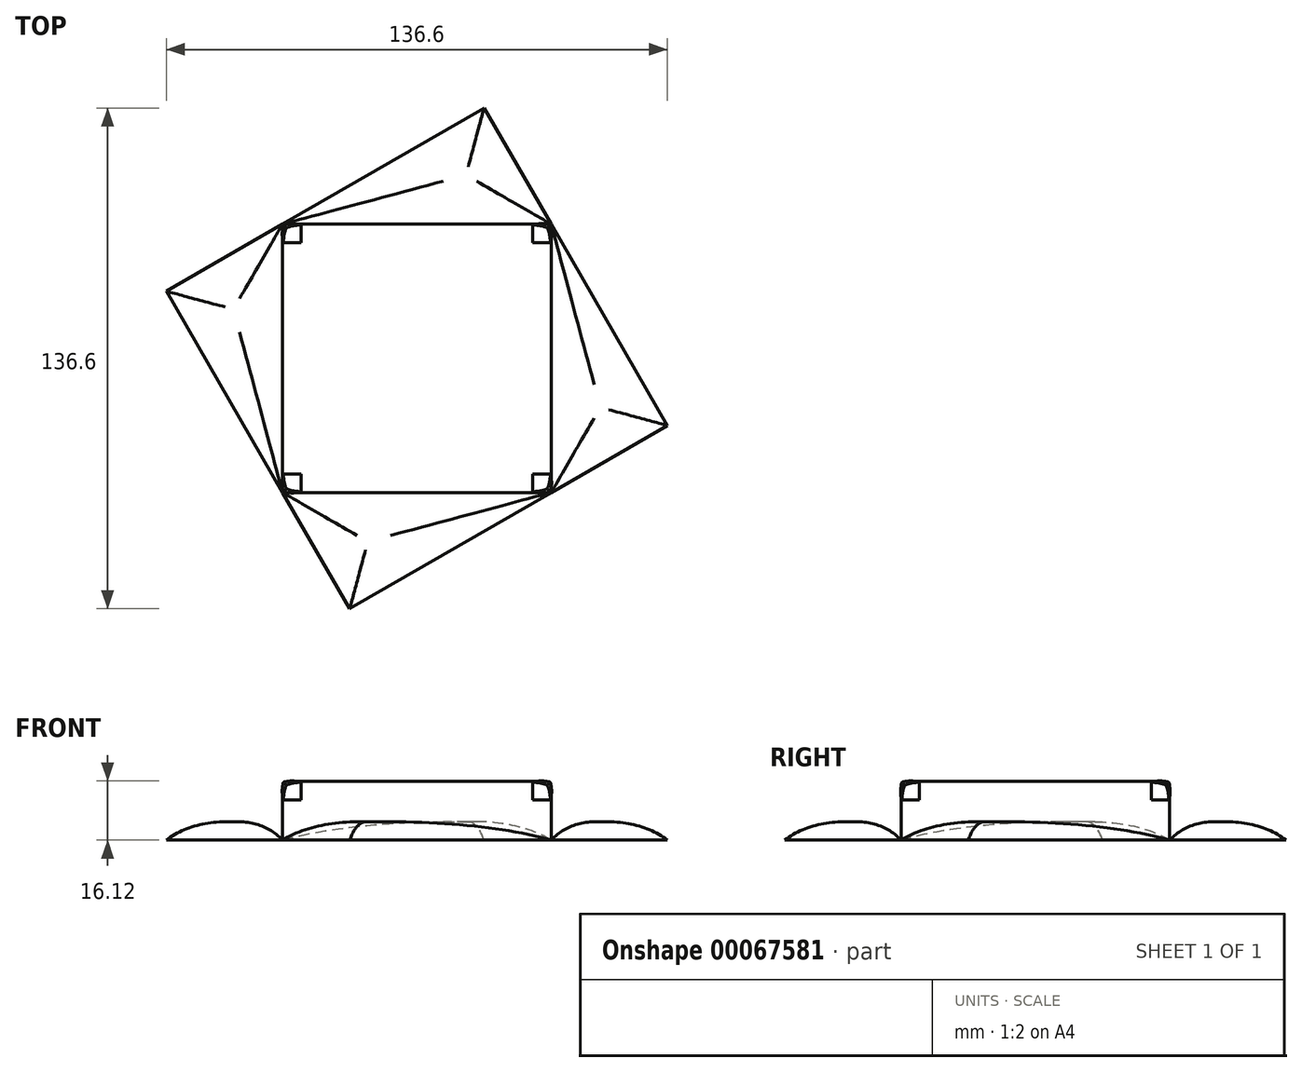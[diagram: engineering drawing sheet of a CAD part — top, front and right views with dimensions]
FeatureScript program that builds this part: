
annotation { "Feature Type Name" : "Feature", "Feature Type Description" : "" }
export const myFeature = defineFeature(function(context is Context, id is Id, definition is map)
    precondition{}
    {
        {
            var Q0;
            Q0=qCreatedBy(makeId("Top.planeOp"),FACE);
            var sketch = newSketch(context, id + "F0", { "sketchPlane" : qUnion([Q0])});
            skLineSegment(sketch, "E0.rect.bottom", {"start": v(36.6, -36.6) * mm, "end": v(-36.6, -36.6) * mm});
            skLineSegment(sketch, "E0.rect.top", {"start": v(36.6, 36.6) * mm, "end": v(-36.6, 36.6) * mm});
            skLineSegment(sketch, "E0.rect.left", {"start": v(36.6, -36.6) * mm, "end": v(36.6, 36.6) * mm});
            skLineSegment(sketch, "E0.rect.right", {"start": v(-36.6, -36.6) * mm, "end": v(-36.6, 36.6) * mm});
            skPoint(sketch, "E0.rect.middle", {"position": v(0, 0) * mm});
            skLineSegment(sketch, "E1", {"start": v(36.6, 36.6) * mm, "end": v(68.3, -18.3) * mm});
            skLineSegment(sketch, "E2", {"start": v(68.3, -18.3) * mm, "end": v(36.6, -36.6) * mm});
            skLineSegment(sketch, "E3.1.0", {"start": v(18.3, 68.3) * mm, "end": v(36.6, 36.6) * mm});
            skLineSegment(sketch, "E3.1.1", {"start": v(-36.6, 36.6) * mm, "end": v(18.3, 68.3) * mm});
            skLineSegment(sketch, "E3.2.0", {"start": v(-68.3, 18.3) * mm, "end": v(-36.6, 36.6) * mm});
            skLineSegment(sketch, "E3.2.1", {"start": v(-36.6, -36.6) * mm, "end": v(-68.3, 18.3) * mm});
            skLineSegment(sketch, "E3.3.0", {"start": v(-18.3, -68.3) * mm, "end": v(-36.6, -36.6) * mm});
            skLineSegment(sketch, "E3.3.1", {"start": v(36.6, -36.6) * mm, "end": v(-18.3, -68.3) * mm});
            skSolve(sketch);
        }
        {
            var Q0;
            Q0=makeQuery(id+"F0.imprint","IMPRINT",FACE,{"disambiguationData":[TD([[makeQuery(id+"F0.imprint","IMPRINT",EDGE,{"derivedFrom":sQuery(id+"F0.wireOp",EDGE,"E0.rect.bottom")}),-1.0]])]});
            extrude(context, id + "F1", {"entities" : qUnion([Q0]), "depth" : 16 * mm});
        }
        {
            var Q0;
            Q0=makeQuery(id+"F0.imprint","IMPRINT",FACE,{"disambiguationData":[TD([[makeQuery(id+"F0.imprint","IMPRINT",EDGE,{"derivedFrom":sQuery(id+"F0.wireOp",EDGE,"E0.rect.right")}),1.0]])]});
            var Q1;
            Q1=makeQuery(id+"F0.imprint","IMPRINT",FACE,{"disambiguationData":[TD([[makeQuery(id+"F0.imprint","IMPRINT",EDGE,{"derivedFrom":sQuery(id+"F0.wireOp",EDGE,"E0.rect.top")}),-1.0]])]});
            var Q2;
            Q2=makeQuery(id+"F0.imprint","IMPRINT",FACE,{"disambiguationData":[TD([[makeQuery(id+"F0.imprint","IMPRINT",EDGE,{"derivedFrom":sQuery(id+"F0.wireOp",EDGE,"E0.rect.left")}),-1.0]])]});
            var Q3;
            Q3=makeQuery(id+"F0.imprint","IMPRINT",FACE,{"disambiguationData":[TD([[makeQuery(id+"F0.imprint","IMPRINT",EDGE,{"derivedFrom":sQuery(id+"F0.wireOp",EDGE,"E0.rect.bottom")}),1.0]])]});
            extrude(context, id + "F2", {"entities" : qUnion([Q0, Q1, Q2, Q3]), "depth" : 5 * mm});
        }
        {
            var Q0;
            Q0=makeQuery(id+"F2.opExtrude","CAP_FACE",FACE,{"disambiguationData":[OSD([sQuery(id+"F0.wireOp",EDGE,"E0.rect.right"),sQuery(id+"F0.wireOp",EDGE,"E3.2.0"),sQuery(id+"F0.wireOp",EDGE,"E3.2.1")])],"isStart":false});
            var Q1;
            Q1=makeQuery(id+"F2.opExtrude","CAP_FACE",FACE,{"disambiguationData":[OSD([sQuery(id+"F0.wireOp",EDGE,"E0.rect.top"),sQuery(id+"F0.wireOp",EDGE,"E3.1.0"),sQuery(id+"F0.wireOp",EDGE,"E3.1.1")])],"isStart":false});
            var Q2;
            Q2=makeQuery(id+"F2.opExtrude","CAP_FACE",FACE,{"disambiguationData":[OSD([sQuery(id+"F0.wireOp",EDGE,"E0.rect.left"),sQuery(id+"F0.wireOp",EDGE,"E1"),sQuery(id+"F0.wireOp",EDGE,"E2")])],"isStart":false});
            var Q3;
            Q3=makeQuery(id+"F2.opExtrude","CAP_FACE",FACE,{"disambiguationData":[OSD([sQuery(id+"F0.wireOp",EDGE,"E0.rect.bottom"),sQuery(id+"F0.wireOp",EDGE,"E3.3.0"),sQuery(id+"F0.wireOp",EDGE,"E3.3.1")])],"isStart":false});
            fillet(context, id + "F3", {"entities" : qUnion([Q0, Q1, Q2, Q3]), "radius" : 16.26 * mm, "tangentPropagation" : true, "allowEdgeOverflow" : false});
        }
        {
            var Q0;
            Q0=makeQuery(id+"F1.opExtrude","CAP_EDGE",EDGE,{"disambiguationData":[OSD([sQuery(id+"F0.wireOp",EDGE,"E0.rect.bottom")])],"isStart":false});
            var Q1;
            Q1=makeQuery(id+"F1.opExtrude","CAP_EDGE",EDGE,{"disambiguationData":[OSD([sQuery(id+"F0.wireOp",EDGE,"E0.rect.right")])],"isStart":false});
            var Q2;
            Q2=makeQuery(id+"F1.opExtrude","CAP_EDGE",EDGE,{"disambiguationData":[OSD([sQuery(id+"F0.wireOp",EDGE,"E0.rect.top")])],"isStart":false});
            var Q3;
            Q3=makeQuery(id+"F1.opExtrude","CAP_EDGE",EDGE,{"disambiguationData":[OSD([sQuery(id+"F0.wireOp",EDGE,"E0.rect.left")])],"isStart":false});
            var Q4;
            Q4=makeQuery(id+"F1.opExtrude","SWEPT_EDGE",EDGE,{"disambiguationData":[OSD([sQuery(id+"F0.wireOp",EDGE,"E0.rect.bottom"),sQuery(id+"F0.wireOp",EDGE,"E0.rect.left"),sQuery(id+"F0.wireOp",EDGE,"E2"),sQuery(id+"F0.wireOp",EDGE,"E3.3.1")])]});
            var Q5;
            Q5=makeQuery(id+"F1.opExtrude","SWEPT_EDGE",EDGE,{"disambiguationData":[OSD([sQuery(id+"F0.wireOp",EDGE,"E0.rect.bottom"),sQuery(id+"F0.wireOp",EDGE,"E0.rect.right"),sQuery(id+"F0.wireOp",EDGE,"E3.2.1"),sQuery(id+"F0.wireOp",EDGE,"E3.3.0")])]});
            var Q6;
            Q6=makeQuery(id+"F1.opExtrude","SWEPT_EDGE",EDGE,{"disambiguationData":[OSD([sQuery(id+"F0.wireOp",EDGE,"E0.rect.top"),sQuery(id+"F0.wireOp",EDGE,"E0.rect.right"),sQuery(id+"F0.wireOp",EDGE,"E3.1.1"),sQuery(id+"F0.wireOp",EDGE,"E3.2.0")])]});
            var Q7;
            Q7=makeQuery(id+"F1.opExtrude","SWEPT_EDGE",EDGE,{"disambiguationData":[OSD([sQuery(id+"F0.wireOp",EDGE,"E0.rect.top"),sQuery(id+"F0.wireOp",EDGE,"E0.rect.left"),sQuery(id+"F0.wireOp",EDGE,"E1"),sQuery(id+"F0.wireOp",EDGE,"E3.1.0")])]});
            fillet(context, id + "F4", {"entities" : qUnion([Q0, Q1, Q2, Q3, Q4, Q5, Q6, Q7]), "radius" : 5 * mm, "tangentPropagation" : true, "rho" : 0.9, "crossSection" : FilletCrossSection.CONIC, "allowEdgeOverflow" : false});
        }
    });
